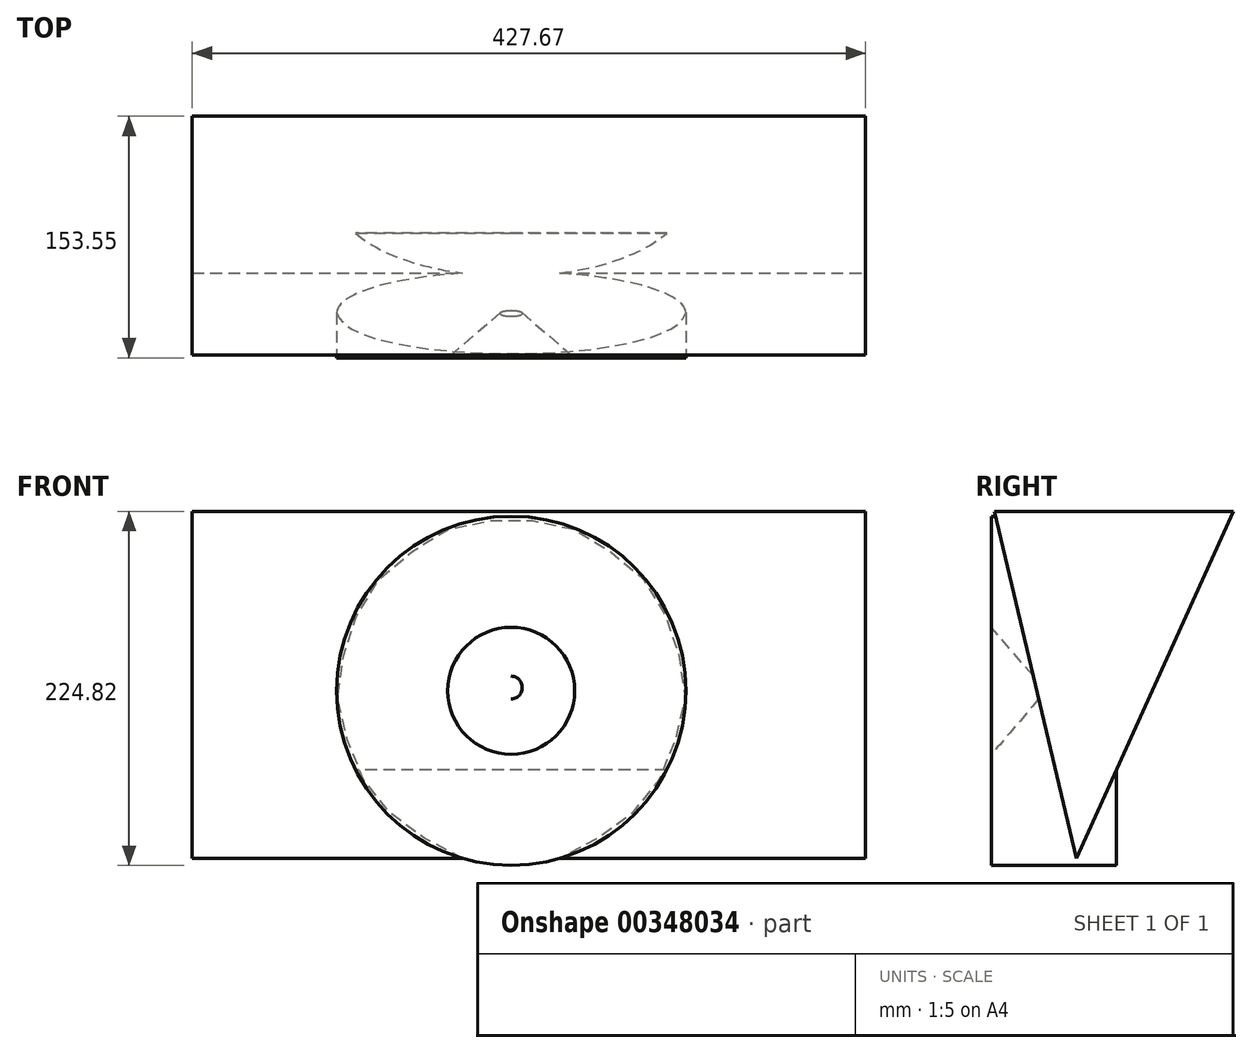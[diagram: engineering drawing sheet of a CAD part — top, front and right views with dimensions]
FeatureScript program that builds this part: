
annotation { "Feature Type Name" : "Feature", "Feature Type Description" : "" }
export const myFeature = defineFeature(function(context is Context, id is Id, definition is map)
    precondition{}
    {
        {
            var Q0;
            Q0=qCreatedBy(makeId("Top.planeOp"),FACE);
            var sketch = newSketch(context, id + "F0", { "sketchPlane" : qUnion([Q0])});
            skLineSegment(sketch, "E0", {"start": v(-0.62, 0.83) * mm, "end": v(46.47, 46.06) * mm});
            skLineSegment(sketch, "E1", {"start": v(46.47, 46.06) * mm, "end": v(109.74, 46.06) * mm});
            skLineSegment(sketch, "E2", {"start": v(109.74, 46.06) * mm, "end": v(109.74, -33.2) * mm});
            skLineSegment(sketch, "E3", {"start": v(109.74, -33.2) * mm, "end": v(39.2, -33.2) * mm});
            skLineSegment(sketch, "E4", {"start": v(39.2, -33.2) * mm, "end": v(-0.62, 0.83) * mm});
            skSolve(sketch);
        }
        {
            var Q0;
            Q0=qCreatedBy(makeId("Top.planeOp"),FACE);
            var sketch = newSketch(context, id + "F1", { "sketchPlane" : qUnion([Q0])});
            skLineSegment(sketch, "E5", {"start": v(-1.12, 1.12) * mm, "end": v(-1.12, 92.84) * mm});
            skSolve(sketch);
        }
        {
            var Q0;
            Q0=makeQuery(id+"F0.imprint","IMPRINT",FACE,{"disambiguationData":[TD([[makeQuery(id+"F0.imprint","IMPRINT",EDGE,{"derivedFrom":sQuery(id+"F0.wireOp",EDGE,"E0")}),-1.0]])]});
            var Q1;
            Q1=sQuery(id+"F1.wireOp",EDGE,"E5");
            revolve(context, id + "F2", {"entities" : qUnion([Q0]), "axis" : qUnion([Q1]), "revolveType" : RevolveType.FULL});
        }
        {
            var Q0;
            Q0=qCreatedBy(makeId("Right.planeOp"),FACE);
            cPlane(context, id + "F3", {"entities" : qUnion([Q0]), "cplaneType" : CPlaneType.OFFSET, "offset" : 223.9 * mm, "width" : 152.4 * mm, "height" : 152.4 * mm});
        }
        {
            var Q0;
            Q0=qCreatedBy(id+"F3.planeOp",FACE);
            var sketch = newSketch(context, id + "F4", { "sketchPlane" : qUnion([Q0])});
            skLineSegment(sketch, "E6", {"start": v(-31.45, 113.95) * mm, "end": v(120.36, 113.95) * mm});
            skLineSegment(sketch, "E7", {"start": v(120.36, 113.95) * mm, "end": v(20.66, -106.5) * mm});
            skLineSegment(sketch, "E8", {"start": v(20.66, -106.5) * mm, "end": v(-31.45, 113.95) * mm});
            skSolve(sketch);
        }
        {
            var Q0;
            Q0=makeQuery(id+"F4.imprint","IMPRINT",FACE,{"disambiguationData":[TD([[makeQuery(id+"F4.imprint","IMPRINT",EDGE,{"derivedFrom":sQuery(id+"F4.wireOp",EDGE,"E6")}),-1.0]])]});
            extrude(context, id + "F5", {"entities" : qUnion([Q0]), "operationType" : NewBodyOperationType.ADD, "oppositeDirection" : true, "depth" : 427.67 * mm});
        }
    });
